# Revit family: R1100-28-G8H-AI
name_source: partatom
category: Plumbing Fixtures
revit_build: Autodesk Revit 2018 (Build: 20170223_1515(x64)
units: mm (PartAtom-declared; Revit-internal decimal feet)

## family parameters
Cut with Voids When Loaded = No
Host = Face
Part Type = Normal
Room Calculation Point = No
Round Connector Dimension = Use Radius
Shared = No

## types (3) — shared parameters
Body Height = 0' - 3 3/4"
Default Elevation = 0' - 0"
Description = GREEN ROOF DRAIN WITH PERFORATED S.S. BALLAST GUARD, AUXILIARY INLET AND REMOVABLE COVER
Floor Drain Material = Paint - Sherwin Williams Paint - #952C2A - Bellwood Red
Manufacturer = MIFAB
Stainless Height = 0' - 8"
URL = WWW.MIFAB.COM
zero-valued in all types: CWFU, WFU

## per-type parameters (varying)
| type | Model | Pipe Diameter | Pipe Radius |
| R1102-28-G8H-AI_2" Drain Pipe Size | R1102-28-G8H-AI | 0' - 2" | 0' - 1" |
| R1103-28-G8H-AI _3" Drain Pipe Size | R1103-28-G8H-AI | 0' - 3" | 0' - 1 1/2" |
| R1104-28-G8H-AI_4" Drain Pipe Size | R1104-28-G8H-AI | 0' - 4" | 0' - 2" |

## geometry (parser evidence)
native form markers: Blend x2, Sweep x8
no freeform markers — native parametric forms only
